# Revit family: E LIGHT -Wallpack (LNC3)
name_source: partatom
category: Lighting Fixtures
revit_build: Autodesk Revit 2016 (Build: 20151007_0715(x64)
units: mm (PartAtom-declared; Revit-internal decimal feet)

## family parameters
Cut with Voids When Loaded = No
Host = Face
Light Source = No
OmniClass Number = 23.80.70.14
OmniClass Title = Luminaries for External Lighting
Part Type = Normal
Room Calculation Point = No
Round Connector Dimension = Use Diameter
Shared = No

## types (7) — shared parameters
Apparent Load = 0 VA
Box = Metal - White
Default Elevation = 48.000"
Description = Midsized LED Wallpack
Glass = Glass - White
Lamp = LED Lamp
Manufacturer = Hubbell Outdoor Lighting
Manufacturer Fax = (866)-898-1065
Model = LNC3
URL = http://www.hubbelloutdoor.com
Voltage = 120 V
Wattage Comments = 62-87W
Watts = 87 W
With Diffuser = Yes

## per-type parameters (varying)
| type | Backbox |
| Bronze | Metal - Bronze |
| Black | Metal - Black |
| White | Metal - White |
| Gray | Metal - Gray |
| Platinum | Metal - Platinum |
| Forest Green | Metal - Forest Green |
| Red | Metal - Red |

## geometry (parser evidence)
native form markers: Sweep x10
no freeform markers — native parametric forms only
